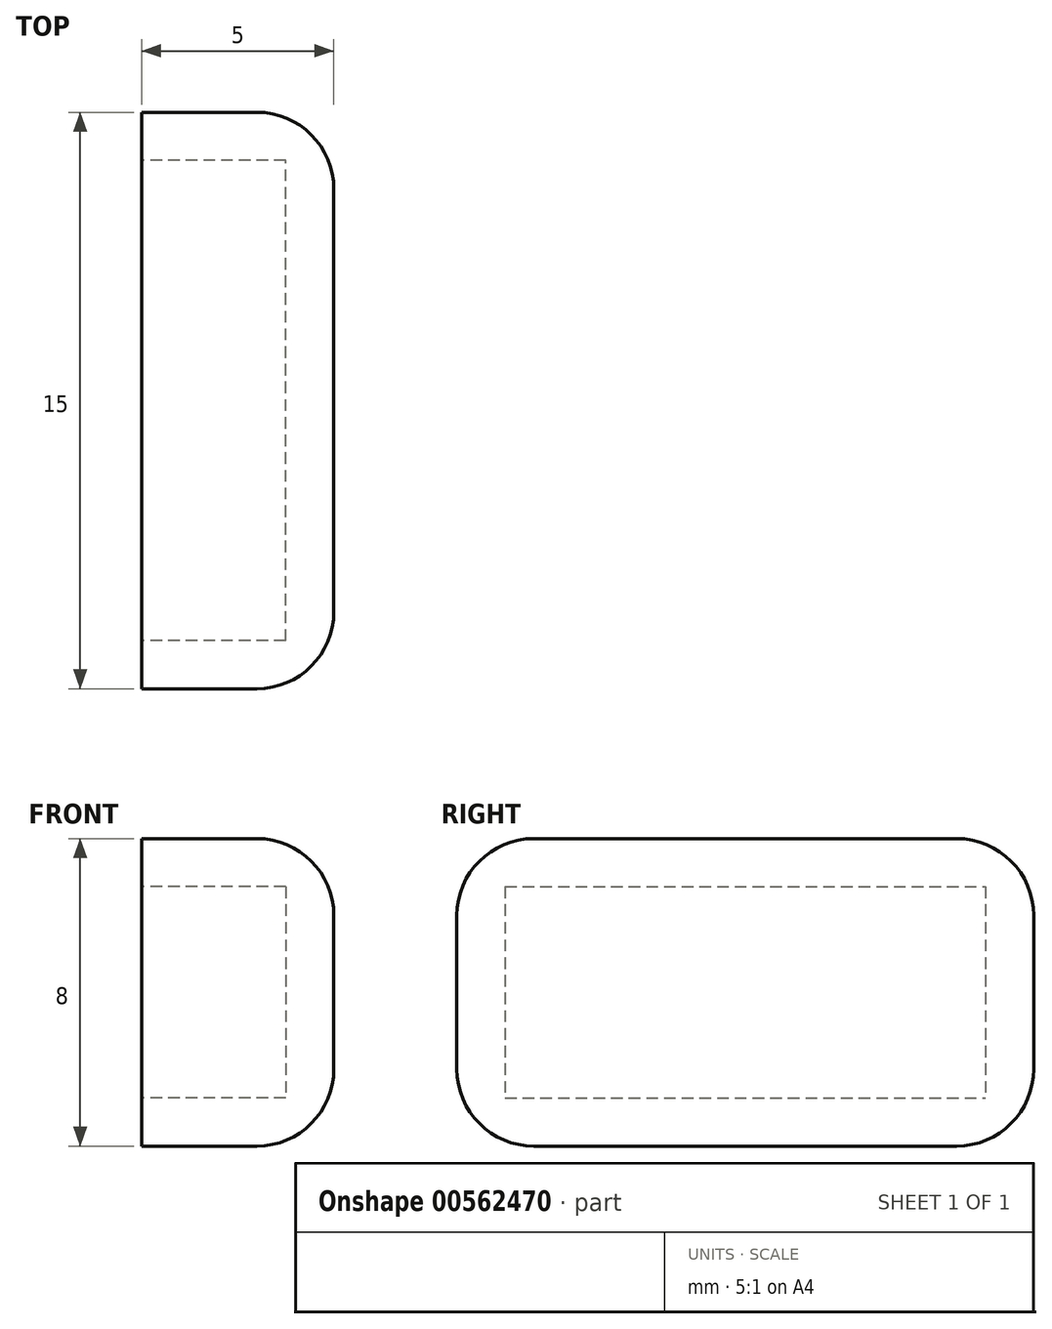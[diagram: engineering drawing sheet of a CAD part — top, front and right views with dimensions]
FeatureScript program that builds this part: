
annotation { "Feature Type Name" : "Feature", "Feature Type Description" : "" }
export const myFeature = defineFeature(function(context is Context, id is Id, definition is map)
    precondition{}
    {
        {
            var Q0;
            Q0=qCreatedBy(makeId("Right.planeOp"),FACE);
            var sketch = newSketch(context, id + "F0", { "sketchPlane" : qUnion([Q0])});
            skLineSegment(sketch, "E0.bottom", {"start": v(-7.5, 4) * mm, "end": v(7.5, 4) * mm});
            skLineSegment(sketch, "E0.top", {"start": v(-7.5, -4) * mm, "end": v(7.5, -4) * mm});
            skLineSegment(sketch, "E0.left", {"start": v(-7.5, 4) * mm, "end": v(-7.5, -4) * mm});
            skLineSegment(sketch, "E0.right", {"start": v(7.5, 4) * mm, "end": v(7.5, -4) * mm});
            skPoint(sketch, "E0.middle", {"position": v(0, 0) * mm});
            skSolve(sketch);
        }
        {
            var Q0;
            Q0=makeQuery(id+"F0.imprint","IMPRINT",FACE,{"disambiguationData":[TD([[makeQuery(id+"F0.imprint","IMPRINT",EDGE,{"derivedFrom":sQuery(id+"F0.wireOp",EDGE,"E0.bottom")}),-1.0]])]});
            extrude(context, id + "F1", {"entities" : qUnion([Q0]), "depth" : 5 * mm, "offsetDistance" : 25 * mm, "symmetric" : true});
        }
        {
            var Q0;
            Q0=makeQuery(id+"F1.opExtrude","CAP_FACE",FACE,{"disambiguationData":[OSD([sQuery(id+"F0.wireOp",EDGE,"E0.bottom"),sQuery(id+"F0.wireOp",EDGE,"E0.top"),sQuery(id+"F0.wireOp",EDGE,"E0.left"),sQuery(id+"F0.wireOp",EDGE,"E0.right")])],"isStart":true});
            var Q1;
            Q1=makeQuery(id+"FFoJCX8bP0vpMuj_1.opExtrude","SWEPT_FACE",FACE,{"disambiguationData":[OSD([sQuery(id+"FLzxutrhiEe1g9o_1.wireOp",EDGE,"RbAp52gx-LZsr-CybZ-8cQ9-zJUY45Q4m9PS.right")])]});
            shell(context, id + "F2", {"entities" : qUnion([Q0, Q1]), "thickness" : 1.25 * mm});
        }
        {
            var Q0;
            Q0=makeQuery(id+"F1.opExtrude","CAP_FACE",FACE,{"disambiguationData":[OSD([sQuery(id+"F0.wireOp",EDGE,"E0.bottom"),sQuery(id+"F0.wireOp",EDGE,"E0.top"),sQuery(id+"F0.wireOp",EDGE,"E0.left"),sQuery(id+"F0.wireOp",EDGE,"E0.right")])],"isStart":false});
            var Q1;
            Q1=makeQuery(id+"F1.opExtrude","SWEPT_EDGE",EDGE,{"disambiguationData":[OSD([sQuery(id+"F0.wireOp",EDGE,"E0.bottom"),sQuery(id+"F0.wireOp",EDGE,"E0.left")])]});
            var Q2;
            Q2=makeQuery(id+"F1.opExtrude","SWEPT_EDGE",EDGE,{"disambiguationData":[OSD([sQuery(id+"F0.wireOp",EDGE,"E0.bottom"),sQuery(id+"F0.wireOp",EDGE,"E0.right")])]});
            var Q3;
            Q3=makeQuery(id+"F1.opExtrude","SWEPT_EDGE",EDGE,{"disambiguationData":[OSD([sQuery(id+"F0.wireOp",EDGE,"E0.top"),sQuery(id+"F0.wireOp",EDGE,"E0.right")])]});
            var Q4;
            Q4=makeQuery(id+"F1.opExtrude","SWEPT_EDGE",EDGE,{"disambiguationData":[OSD([sQuery(id+"F0.wireOp",EDGE,"E0.top"),sQuery(id+"F0.wireOp",EDGE,"E0.left")])]});
            var Q5;
            Q5=makeQuery(id+"FFoJCX8bP0vpMuj_1.opExtrude","CAP_EDGE",EDGE,{"disambiguationData":[OSD([sQuery(id+"FLzxutrhiEe1g9o_1.wireOp",EDGE,"RbAp52gx-LZsr-CybZ-8cQ9-zJUY45Q4m9PS.left")])],"isStart":false});
            var Q6;
            Q6=makeQuery(id+"FFoJCX8bP0vpMuj_1.opExtrude","CAP_EDGE",EDGE,{"disambiguationData":[OSD([sQuery(id+"FLzxutrhiEe1g9o_1.wireOp",EDGE,"RbAp52gx-LZsr-CybZ-8cQ9-zJUY45Q4m9PS.top")])],"isStart":false});
            var Q7;
            Q7=makeQuery(id+"FFoJCX8bP0vpMuj_1.opExtrude","CAP_EDGE",EDGE,{"disambiguationData":[OSD([sQuery(id+"FLzxutrhiEe1g9o_1.wireOp",EDGE,"RbAp52gx-LZsr-CybZ-8cQ9-zJUY45Q4m9PS.bottom")])],"isStart":false});
            fillet(context, id + "F3", {"entities" : qUnion([Q0, Q1, Q2, Q3, Q4, Q5, Q6, Q7]), "radius" : 2 * mm, "tangentPropagation" : true, "allowEdgeOverflow" : false});
        }
    });
